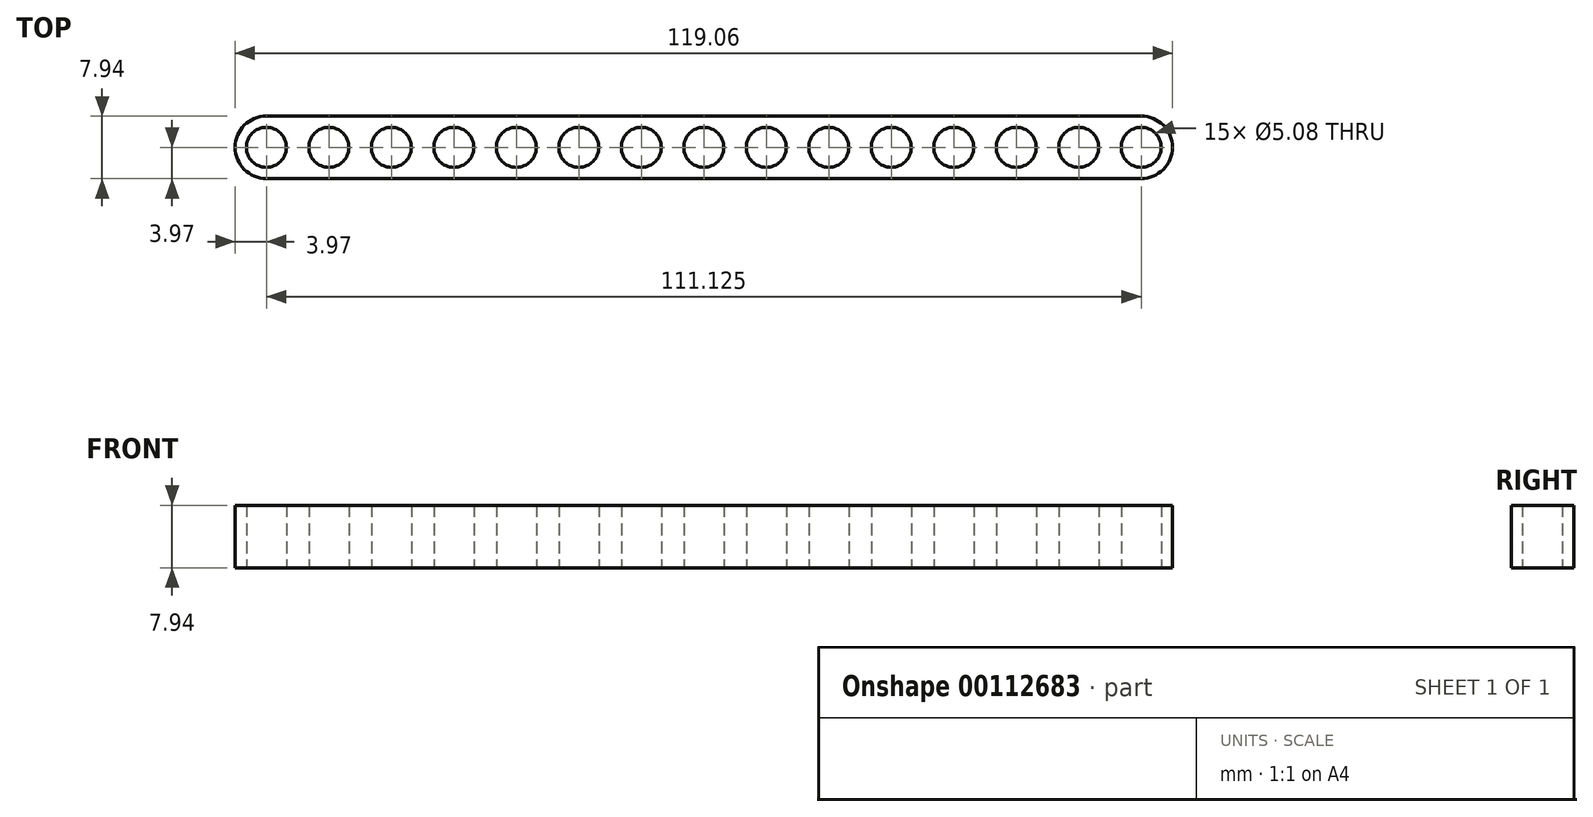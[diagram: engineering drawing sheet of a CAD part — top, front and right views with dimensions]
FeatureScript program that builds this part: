
annotation { "Feature Type Name" : "Feature", "Feature Type Description" : "" }
export const myFeature = defineFeature(function(context is Context, id is Id, definition is map)
    precondition{}
    {
        {
            var Q0;
            Q0=qCreatedBy(makeId("Top.planeOp"),FACE);
            var sketch = newSketch(context, id + "F0", { "sketchPlane" : qUnion([Q0])});
            skLineSegment(sketch, "E0", {"start": v(0, 0) * mm, "end": v(7.94, 0) * mm, "construction": true});
            skLineSegment(sketch, "E1", {"start": v(7.94, 0) * mm, "end": v(15.88, 0) * mm, "construction": true});
            skLineSegment(sketch, "E2", {"start": v(15.88, 0) * mm, "end": v(23.81, 0) * mm, "construction": true});
            skLineSegment(sketch, "E3", {"start": v(23.81, 0) * mm, "end": v(31.75, 0) * mm, "construction": true});
            skLineSegment(sketch, "E4.bottom", {"start": v(0, 3.97) * mm, "end": v(111.12, 3.97) * mm});
            skLineSegment(sketch, "E4.top", {"start": v(0, -3.97) * mm, "end": v(111.12, -3.97) * mm});
            skLineSegment(sketch, "E4.left", {"start": v(0, 3.97) * mm, "end": v(0, -3.97) * mm});
            skLineSegment(sketch, "E4.right", {"start": v(111.12, 3.97) * mm, "end": v(111.12, -3.97) * mm});
            skArc(sketch, "E5", {"start": v(0, 3.97) * mm, "mid": v(-3.97, 0) * mm, "end": v(0, -3.97) * mm});
            skArc(sketch, "E6", {"start": v(111.12, -3.97) * mm, "mid": v(115.1, 0) * mm, "end": v(111.12, 3.97) * mm});
            skCircle(sketch, "E7", {"center": v(0, 0) * mm, "radius": 2.54 * mm});
            skCircle(sketch, "E8", {"center": v(7.94, 0) * mm, "radius": 2.54 * mm});
            skCircle(sketch, "E9", {"center": v(15.88, 0) * mm, "radius": 2.54 * mm});
            skCircle(sketch, "E10", {"center": v(23.81, 0) * mm, "radius": 2.54 * mm});
            skCircle(sketch, "E11", {"center": v(31.75, 0) * mm, "radius": 2.54 * mm});
            skLineSegment(sketch, "E12", {"start": v(31.75, 0) * mm, "end": v(39.69, 0) * mm, "construction": true});
            skLineSegment(sketch, "E13", {"start": v(39.69, 0) * mm, "end": v(47.62, 0) * mm, "construction": true});
            skLineSegment(sketch, "E14", {"start": v(47.62, 0) * mm, "end": v(55.56, 0) * mm, "construction": true});
            skLineSegment(sketch, "E15", {"start": v(55.56, 0) * mm, "end": v(63.5, 0) * mm, "construction": true});
            skCircle(sketch, "E16", {"center": v(39.69, 0) * mm, "radius": 2.54 * mm});
            skCircle(sketch, "E17", {"center": v(47.62, 0) * mm, "radius": 2.54 * mm});
            skCircle(sketch, "E18", {"center": v(55.56, 0) * mm, "radius": 2.54 * mm});
            skCircle(sketch, "E19", {"center": v(63.5, 0) * mm, "radius": 2.54 * mm});
            skLineSegment(sketch, "E20", {"start": v(63.5, 0) * mm, "end": v(71.44, 0) * mm, "construction": true});
            skLineSegment(sketch, "E21", {"start": v(71.44, 0) * mm, "end": v(79.38, 0) * mm, "construction": true});
            skLineSegment(sketch, "E22", {"start": v(79.38, 0) * mm, "end": v(87.31, 0) * mm, "construction": true});
            skLineSegment(sketch, "E23", {"start": v(87.31, 0) * mm, "end": v(95.25, 0) * mm, "construction": true});
            skCircle(sketch, "E24", {"center": v(71.44, 0) * mm, "radius": 2.54 * mm});
            skCircle(sketch, "E25", {"center": v(79.38, 0) * mm, "radius": 2.54 * mm});
            skCircle(sketch, "E26", {"center": v(87.31, 0) * mm, "radius": 2.54 * mm});
            skCircle(sketch, "E27", {"center": v(95.25, 0) * mm, "radius": 2.54 * mm});
            skLineSegment(sketch, "E28", {"start": v(95.25, 0) * mm, "end": v(103.19, 0) * mm, "construction": true});
            skLineSegment(sketch, "E29", {"start": v(103.19, 0) * mm, "end": v(111.12, 0) * mm, "construction": true});
            skCircle(sketch, "E30", {"center": v(103.19, 0) * mm, "radius": 2.54 * mm});
            skCircle(sketch, "E31", {"center": v(111.12, 0) * mm, "radius": 2.54 * mm});
            skSolve(sketch);
        }
        {
            var Q0;
            Q0=qSketchRegion(id+"F0",true);
            extrude(context, id + "F1", {"entities" : qUnion([Q0]), "depth" : 7.94 * mm});
        }
    });
